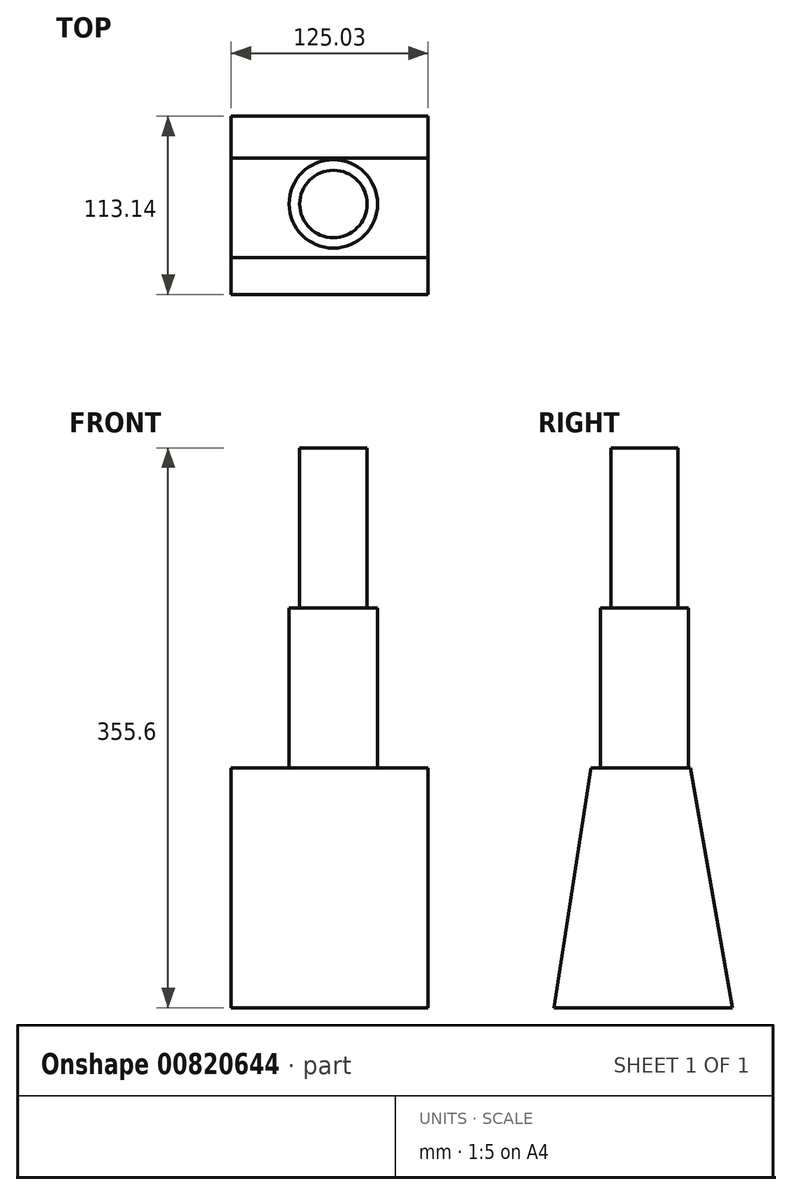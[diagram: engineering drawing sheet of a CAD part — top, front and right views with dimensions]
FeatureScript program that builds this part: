
annotation { "Feature Type Name" : "Feature", "Feature Type Description" : "" }
export const myFeature = defineFeature(function(context is Context, id is Id, definition is map)
    precondition{}
    {
        {
            var Q0;
            Q0=qCreatedBy(makeId("Top.planeOp"),FACE);
            var sketch = newSketch(context, id + "F0", { "sketchPlane" : qUnion([Q0])});
            skLineSegment(sketch, "E0.bottom", {"start": v(-64.86, 55.73) * mm, "end": v(60.17, 55.73) * mm});
            skLineSegment(sketch, "E0.top", {"start": v(-64.86, -57.4) * mm, "end": v(60.17, -57.4) * mm});
            skLineSegment(sketch, "E0.left", {"start": v(-64.86, 55.73) * mm, "end": v(-64.86, -57.4) * mm});
            skLineSegment(sketch, "E0.right", {"start": v(60.17, 55.73) * mm, "end": v(60.17, -57.4) * mm});
            skSolve(sketch);
        }
        {
            var Q0;
            Q0 = qSketchRegion(id + "F0", true);
            extrude(context, id + "F1", {"entities" : qUnion([Q0]), "depth" : 152.4 * mm, "offsetDistance" : 25.4 * mm});
        }
        {
            var Q0;
            Q0=makeQuery(id+"F1.opExtrude","SWEPT_FACE",FACE,{"disambiguationData":[OSD([sQuery(id+"F0.wireOp",EDGE,"E0.right")])]});
            var sketch = newSketch(context, id + "F2", { "sketchPlane" : qUnion([Q0])});
            skLineSegment(sketch, "E1", {"start": v(-57.4, 0) * mm, "end": v(-33.92, 152.4) * mm});
            skLineSegment(sketch, "E2", {"start": v(-33.92, 152.4) * mm, "end": v(-57.4, 152.4) * mm});
            skLineSegment(sketch, "E3", {"start": v(-57.4, 152.4) * mm, "end": v(-57.4, 0) * mm});
            skSolve(sketch);
        }
        {
            var Q0;
            Q0 = qSketchRegion(id + "F2", true);
            extrude(context, id + "F3", {"entities" : qUnion([Q0]), "operationType" : NewBodyOperationType.REMOVE, "endBound" : BoundingType.THROUGH_ALL, "oppositeDirection" : true, "depth" : 25.4 * mm, "offsetDistance" : 25.4 * mm});
        }
        {
            var Q0;
            Q0=makeQuery(id+"F1.opExtrude","SWEPT_FACE",FACE,{"disambiguationData":[OSD([sQuery(id+"F0.wireOp",EDGE,"E0.right")])]});
            var sketch = newSketch(context, id + "F4", { "sketchPlane" : qUnion([Q0])});
            skLineSegment(sketch, "E4", {"start": v(55.73, 0) * mm, "end": v(29.23, 152.4) * mm});
            skLineSegment(sketch, "E5", {"start": v(29.23, 152.4) * mm, "end": v(55.73, 152.4) * mm});
            skLineSegment(sketch, "E6", {"start": v(55.73, 152.4) * mm, "end": v(55.73, 0) * mm});
            skSolve(sketch);
        }
        {
            var Q0;
            Q0 = qSketchRegion(id + "F4", true);
            extrude(context, id + "F5", {"entities" : qUnion([Q0]), "operationType" : NewBodyOperationType.REMOVE, "endBound" : BoundingType.THROUGH_ALL, "oppositeDirection" : true, "depth" : 25.4 * mm, "offsetDistance" : 25.4 * mm});
        }
        {
            var Q0;
            Q0=makeQuery(id+"F1.opExtrude","CAP_FACE",FACE,{"disambiguationData":[OSD([sQuery(id+"F0.wireOp",EDGE,"E0.bottom"),sQuery(id+"F0.wireOp",EDGE,"E0.top"),sQuery(id+"F0.wireOp",EDGE,"E0.left"),sQuery(id+"F0.wireOp",EDGE,"E0.right")])],"isStart":false});
            var sketch = newSketch(context, id + "F6", { "sketchPlane" : qUnion([Q0])});
            skCircle(sketch, "E7", {"center": v(0, 0) * mm, "radius": 28.06 * mm});
            skSolve(sketch);
        }
        {
            var Q0;
            Q0 = qSketchRegion(id + "F6", true);
            extrude(context, id + "F7", {"entities" : qUnion([Q0]), "operationType" : NewBodyOperationType.ADD, "depth" : 101.6 * mm, "offsetDistance" : 25.4 * mm});
        }
        {
            var Q0;
            Q0=makeQuery(id+"F7.opExtrude","CAP_FACE",FACE,{"disambiguationData":[OSD([sQuery(id+"F6.wireOp",EDGE,"E7")])],"isStart":false});
            var sketch = newSketch(context, id + "F8", { "sketchPlane" : qUnion([Q0])});
            skCircle(sketch, "E8", {"center": v(0, 0) * mm, "radius": 21.42 * mm});
            skSolve(sketch);
        }
        {
            var Q0;
            Q0 = qSketchRegion(id + "F8", true);
            extrude(context, id + "F9", {"entities" : qUnion([Q0]), "operationType" : NewBodyOperationType.ADD, "depth" : 101.6 * mm, "offsetDistance" : 25.4 * mm});
        }
    });
